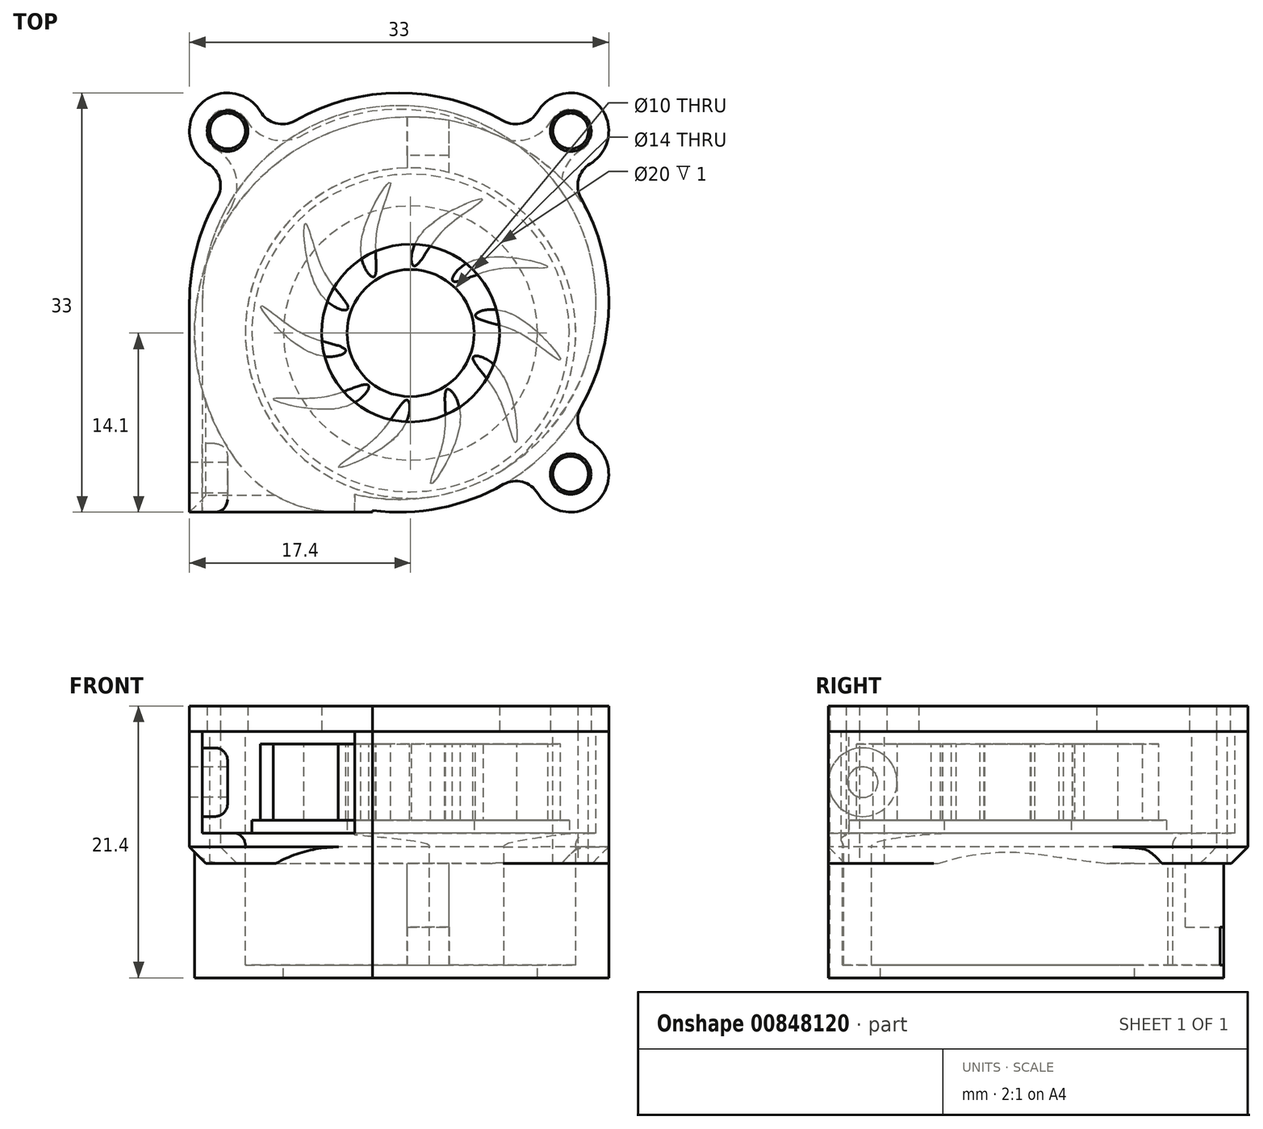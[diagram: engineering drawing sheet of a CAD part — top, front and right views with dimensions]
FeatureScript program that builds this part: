
annotation { "Feature Type Name" : "Feature", "Feature Type Description" : "" }
export const myFeature = defineFeature(function(context is Context, id is Id, definition is map)
    precondition{}
    {
        {
            var Q0;
            Q0=qCreatedBy(makeId("Top.planeOp"),FACE);
            var sketch = newSketch(context, id + "F0", { "sketchPlane" : qUnion([Q0])});
            skLineSegment(sketch, "E0.bottom", {"start": v(-16.5, 16.5) * mm, "end": v(16.5, 16.5) * mm});
            skLineSegment(sketch, "E0.top", {"start": v(-16.5, -16.5) * mm, "end": v(16.5, -16.5) * mm});
            skLineSegment(sketch, "E0.left", {"start": v(-16.5, 16.5) * mm, "end": v(-16.5, -16.5) * mm});
            skLineSegment(sketch, "E0.right", {"start": v(16.5, 16.5) * mm, "end": v(16.5, -16.5) * mm});
            skPoint(sketch, "E0.middle", {"position": v(0, 0) * mm});
            skCircle(sketch, "E1", {"center": v(0.9, -2.4) * mm, "radius": 13 * mm});
            skPoint(sketch, "E2.positionSnap0", {"position": v(0, -16.5) * mm});
            skArc(sketch, "E3", {"start": v(-3.5, -15.1) * mm, "mid": v(12.13, 9.64) * mm, "end": v(-15.5, 0) * mm});
            skLineSegment(sketch, "E4", {"start": v(-15.5, 0) * mm, "end": v(-15.5, -16.5) * mm});
            skLineSegment(sketch, "E5", {"start": v(-3.5, -16.5) * mm, "end": v(-3.5, -15.1) * mm});
            skLineSegment(sketch, "E6.bottom", {"start": v(13.5, 13.5) * mm, "end": v(-13.5, 13.5) * mm, "construction": true});
            skLineSegment(sketch, "E6.top", {"start": v(13.5, -13.5) * mm, "end": v(-13.5, -13.5) * mm, "construction": true});
            skLineSegment(sketch, "E6.left", {"start": v(13.5, 13.5) * mm, "end": v(13.5, -13.5) * mm, "construction": true});
            skLineSegment(sketch, "E6.right", {"start": v(-13.5, 13.5) * mm, "end": v(-13.5, -13.5) * mm, "construction": true});
            skCircle(sketch, "E7", {"center": v(-13.5, 13.5) * mm, "radius": 1.4 * mm});
            skCircle(sketch, "E8", {"center": v(13.5, 13.5) * mm, "radius": 1.4 * mm});
            skCircle(sketch, "E9", {"center": v(13.5, -13.5) * mm, "radius": 1.4 * mm});
            skCircle(sketch, "E10", {"center": v(0.9, -2.4) * mm, "radius": 11.75 * mm, "construction": true});
            skArc(sketch, "E11.0", {"start": v(-2.1, -16.37) * mm, "mid": v(12.39, 10.9) * mm, "end": v(-16.5, 0) * mm});
            skLineSegment(sketch, "E12", {"start": v(-2.1, -16.37) * mm, "end": v(-2.1, -16.5) * mm});
            skArc(sketch, "E13", {"start": v(-10.63, 12.62) * mm, "mid": v(-15.62, 15.62) * mm, "end": v(-12.62, 10.63) * mm});
            skArc(sketch, "E14.1.0", {"start": v(12.62, 10.63) * mm, "mid": v(15.62, 15.62) * mm, "end": v(10.63, 12.62) * mm});
            skArc(sketch, "E14.2.0", {"start": v(10.63, -12.62) * mm, "mid": v(15.62, -15.62) * mm, "end": v(12.62, -10.63) * mm});
            skLineSegment(sketch, "E14.anchor1", {"start": v(0, 0) * mm, "end": v(-12.62, 10.63) * mm, "construction": true});
            skLineSegment(sketch, "E14.anchor2", {"start": v(0, 0) * mm, "end": v(12.62, -10.63) * mm, "construction": true});
            skLineSegment(sketch, "E15", {"start": v(3.93, 10.24) * mm, "end": v(3.93, 11.58) * mm});
            skLineSegment(sketch, "E16", {"start": v(3.93, 11.58) * mm, "end": v(0.64, 11.58) * mm});
            skLineSegment(sketch, "E17", {"start": v(0.64, 11.58) * mm, "end": v(0.64, 10.6) * mm});
            skSolve(sketch);
        }
        {
            var Q0;
            {var subQ0=sQuery(id+"F0.wireOp",EDGE,"8aHMBO7B-eonY-Z6f1-7xxv-SSlK2QK2lGQh");Q0=makeQuery(id+"F0.imprint","IMPRINT",FACE,{"disambiguationData":[TD([[makeQuery(id+"F0.imprint","IMPRINT",EDGE,{"derivedFrom":subQ0}),1.0]])]});}
            var Q1;
            {var subQ0=sQuery(id+"F0.wireOp",EDGE,"mYrk5g2D-YhFv-AHOF-tiMq-TT1jAZq6Yysg");Q1=makeQuery(id+"F0.imprint","IMPRINT",FACE,{"disambiguationData":[TD([[makeQuery(id+"F0.imprint","IMPRINT",EDGE,{"derivedFrom":subQ0}),1.0]])]});}
            var Q2;
            {var subQ0=sQuery(id+"F0.wireOp",EDGE,"RpQWQKDe-v6hF-UeJ0-nlzF-b0iv6W1jkAfd");Q2=makeQuery(id+"F0.imprint","IMPRINT",FACE,{"disambiguationData":[TD([[makeQuery(id+"F0.imprint","IMPRINT",EDGE,{"derivedFrom":subQ0}),-1.0]])]});}
            var Q3;
            Q3=makeQuery(id+"F0.imprint","IMPRINT",FACE,{"disambiguationData":[TD([[makeQuery(id+"F0.imprint","IMPRINT",EDGE,{"derivedFrom":sQuery(id+"F0.wireOp",EDGE,"E7")}),-1.0]])]});
            var Q4;
            Q4=makeQuery(id+"F0.imprint","IMPRINT",FACE,{"disambiguationData":[TD([[makeQuery(id+"F0.imprint","IMPRINT",EDGE,{"derivedFrom":sQuery(id+"F0.wireOp",EDGE,"E3")}),-1.0]])]});
            var Q5;
            Q5=makeQuery(id+"F0.imprint","IMPRINT",FACE,{"disambiguationData":[TD([[makeQuery(id+"F0.imprint","IMPRINT",EDGE,{"derivedFrom":sQuery(id+"F0.wireOp",EDGE,"E8")}),-1.0]])]});
            var Q6;
            Q6=makeQuery(id+"F0.imprint","IMPRINT",FACE,{"disambiguationData":[TD([[makeQuery(id+"F0.imprint","IMPRINT",EDGE,{"derivedFrom":sQuery(id+"F0.wireOp",EDGE,"E9")}),-1.0]])]});
            var Q7;
            Q7=makeQuery(id+"F0.imprint","IMPRINT",FACE,{"disambiguationData":[TD([[makeQuery(id+"F0.imprint","IMPRINT",EDGE,{"derivedFrom":sQuery(id+"F0.wireOp",EDGE,"E3")}),1.0]])]});
            var Q8;
            {var subQ0=sQuery(id+"F0.wireOp",EDGE,"E15");Q8=makeQuery(id+"F0.imprint","IMPRINT",FACE,{"disambiguationData":[TD([[makeQuery(id+"F0.imprint","IMPRINT",EDGE,{"derivedFrom":subQ0}),1.0]])]});}
            var Q9;
            {var subQ5=sQuery(id+"F0.wireOp",EDGE,"E4");Q9=makeQuery(id+"F0.imprint","IMPRINT",FACE,{"disambiguationData":[TD([[makeQuery(id+"F0.imprint","IMPRINT",EDGE,{"derivedFrom":subQ5}),-1.0]])]});}
            extrude(context, id + "F1", {"entities" : qUnion([Q0, Q1, Q2, Q3, Q4, Q5, Q6, Q7, Q8, Q9]), "oppositeDirection" : true, "depth" : 2.4 * mm, "offsetDistance" : 25 * mm});
        }
        {
            var Q0;
            Q0=makeQuery(id+"F0.imprint","IMPRINT",FACE,{"disambiguationData":[TD([[makeQuery(id+"F0.imprint","IMPRINT",EDGE,{"derivedFrom":sQuery(id+"F0.wireOp",EDGE,"E7")}),-1.0]])]});
            var Q1;
            Q1=makeQuery(id+"F0.imprint","IMPRINT",FACE,{"disambiguationData":[TD([[makeQuery(id+"F0.imprint","IMPRINT",EDGE,{"derivedFrom":sQuery(id+"F0.wireOp",EDGE,"E3")}),-1.0]])]});
            var Q2;
            Q2=makeQuery(id+"F0.imprint","IMPRINT",FACE,{"disambiguationData":[TD([[makeQuery(id+"F0.imprint","IMPRINT",EDGE,{"derivedFrom":sQuery(id+"F0.wireOp",EDGE,"E9")}),-1.0]])]});
            var Q3;
            Q3=makeQuery(id+"F0.imprint","IMPRINT",FACE,{"disambiguationData":[TD([[makeQuery(id+"F0.imprint","IMPRINT",EDGE,{"derivedFrom":sQuery(id+"F0.wireOp",EDGE,"E8")}),-1.0]])]});
            var Q4;
            {var subQ5=sQuery(id+"F0.wireOp",EDGE,"E4");Q4=makeQuery(id+"F0.imprint","IMPRINT",FACE,{"disambiguationData":[TD([[makeQuery(id+"F0.imprint","IMPRINT",EDGE,{"derivedFrom":subQ5}),-1.0]])]});}
            extrude(context, id + "F2", {"entities" : qUnion([Q0, Q1, Q2, Q3, Q4]), "operationType" : NewBodyOperationType.ADD, "depth" : 8 * mm, "offsetDistance" : 25 * mm});
        }
        {
            var Q0;
            Q0=makeQuery(id+"F1.opExtrude","CAP_FACE",FACE,{"disambiguationData":[OSD([sQuery(id+"F0.wireOp",EDGE,"E0.bottom"),sQuery(id+"F0.wireOp",EDGE,"E0.top"),sQuery(id+"F0.wireOp",EDGE,"E0.left"),sQuery(id+"F0.wireOp",EDGE,"E0.right"),sQuery(id+"F0.wireOp",EDGE,"E1"),sQuery(id+"F0.wireOp",EDGE,"E7"),sQuery(id+"F0.wireOp",EDGE,"E8"),sQuery(id+"F0.wireOp",EDGE,"E9")])],"isStart":false});
            var sketch = newSketch(context, id + "F3", { "sketchPlane" : qUnion([Q0])});
            skCircle(sketch, "E18.0", {"center": v(0.9, 2.4) * mm, "radius": 17 * mm});
            skArc(sketch, "E19.0", {"start": v(-2.1, 16.37) * mm, "mid": v(12.39, -10.9) * mm, "end": v(-16.5, 0) * mm});
            skLineSegment(sketch, "E20.0", {"start": v(3.93, -11.58) * mm, "end": v(0.64, -11.58) * mm});
            skLineSegment(sketch, "E21.0", {"start": v(3.93, -10.24) * mm, "end": v(3.93, -11.58) * mm});
            skPoint(sketch, "E22.0", {"position": v(0.64, -11.09) * mm});
            skLineSegment(sketch, "E23.0", {"start": v(0.64, -11.58) * mm, "end": v(0.64, -10.6) * mm});
            skSolve(sketch);
        }
        {
            var Q0;
            Q0=makeQuery(id+"F3.imprint","IMPRINT",FACE,{"disambiguationData":[TD([[makeQuery(id+"F3.imprint","IMPRINT",EDGE,{"derivedFrom":sQuery(id+"F3.wireOp",EDGE,"E20.0")}),1.0]])]});
            extrude(context, id + "F4", {"entities" : qUnion([Q0]), "operationType" : NewBodyOperationType.ADD, "depth" : 8 * mm, "offsetDistance" : 25 * mm});
        }
        {
            var Q0;
            {var subQ0=sQuery(id+"F0.wireOp",EDGE,"E13");var subQ1=sQuery(id+"F0.wireOp",EDGE,"E11.0");var subQ2=makeQuery(id+"F0.imprint","INTERSECT",VERTEX,{"disambiguationData":[OD(1.0)],"derivedFrom":[subQ1,subQ0]});Q0=makeQuery(id+"F2.boolean.opBoolean","MERGE",EDGE,{"derivedFrom":[makeQuery(id+"F1.opExtrude","SWEPT_EDGE",EDGE,{"disambiguationData":[OSD([subQ1,subQ0]),TDD([subQ2])]}),makeQuery(id+"F2.opExtrude","SWEPT_EDGE",EDGE,{"disambiguationData":[OSD([subQ1,subQ0]),TDD([subQ2])]})]});}
            var Q1;
            {var subQ0=sQuery(id+"F0.wireOp",EDGE,"E13");var subQ1=sQuery(id+"F0.wireOp",EDGE,"E11.0");var subQ2=makeQuery(id+"F0.imprint","INTERSECT",VERTEX,{"disambiguationData":[OD(0.0)],"derivedFrom":[subQ1,subQ0]});Q1=makeQuery(id+"F2.boolean.opBoolean","MERGE",EDGE,{"derivedFrom":[makeQuery(id+"F1.opExtrude","SWEPT_EDGE",EDGE,{"disambiguationData":[OSD([subQ1,subQ0]),TDD([subQ2])]}),makeQuery(id+"F2.opExtrude","SWEPT_EDGE",EDGE,{"disambiguationData":[OSD([subQ1,subQ0]),TDD([subQ2])]})]});}
            var Q2;
            {var subQ0=sQuery(id+"F0.wireOp",EDGE,"E14.1.0");var subQ1=sQuery(id+"F0.wireOp",EDGE,"E11.0");var subQ2=makeQuery(id+"F0.imprint","INTERSECT",VERTEX,{"disambiguationData":[OD(1.0)],"derivedFrom":[subQ1,subQ0]});Q2=makeQuery(id+"F2.boolean.opBoolean","MERGE",EDGE,{"derivedFrom":[makeQuery(id+"F1.opExtrude","SWEPT_EDGE",EDGE,{"disambiguationData":[OSD([subQ1,subQ0]),TDD([subQ2])]}),makeQuery(id+"F2.opExtrude","SWEPT_EDGE",EDGE,{"disambiguationData":[OSD([subQ1,subQ0]),TDD([subQ2])]})]});}
            var Q3;
            {var subQ0=sQuery(id+"F0.wireOp",EDGE,"E14.1.0");var subQ1=sQuery(id+"F0.wireOp",EDGE,"E11.0");var subQ2=makeQuery(id+"F0.imprint","INTERSECT",VERTEX,{"disambiguationData":[OD(0.0)],"derivedFrom":[subQ1,subQ0]});Q3=makeQuery(id+"F2.boolean.opBoolean","MERGE",EDGE,{"derivedFrom":[makeQuery(id+"F1.opExtrude","SWEPT_EDGE",EDGE,{"disambiguationData":[OSD([subQ1,subQ0]),TDD([subQ2])]}),makeQuery(id+"F2.opExtrude","SWEPT_EDGE",EDGE,{"disambiguationData":[OSD([subQ1,subQ0]),TDD([subQ2])]})]});}
            var Q4;
            {var subQ0=sQuery(id+"F0.wireOp",EDGE,"E14.2.0");var subQ1=sQuery(id+"F0.wireOp",EDGE,"E11.0");var subQ2=makeQuery(id+"F0.imprint","INTERSECT",VERTEX,{"disambiguationData":[OD(0.0)],"derivedFrom":[subQ1,subQ0]});Q4=makeQuery(id+"F2.boolean.opBoolean","MERGE",EDGE,{"derivedFrom":[makeQuery(id+"F1.opExtrude","SWEPT_EDGE",EDGE,{"disambiguationData":[OSD([subQ1,subQ0]),TDD([subQ2])]}),makeQuery(id+"F2.opExtrude","SWEPT_EDGE",EDGE,{"disambiguationData":[OSD([subQ1,subQ0]),TDD([subQ2])]})]});}
            var Q5;
            {var subQ0=sQuery(id+"F0.wireOp",EDGE,"E14.2.0");var subQ1=sQuery(id+"F0.wireOp",EDGE,"E11.0");var subQ2=makeQuery(id+"F0.imprint","INTERSECT",VERTEX,{"disambiguationData":[OD(1.0)],"derivedFrom":[subQ1,subQ0]});Q5=makeQuery(id+"F2.boolean.opBoolean","MERGE",EDGE,{"derivedFrom":[makeQuery(id+"F1.opExtrude","SWEPT_EDGE",EDGE,{"disambiguationData":[OSD([subQ1,subQ0]),TDD([subQ2])]}),makeQuery(id+"F2.opExtrude","SWEPT_EDGE",EDGE,{"disambiguationData":[OSD([subQ1,subQ0]),TDD([subQ2])]})]});}
            fillet(context, id + "F5", {"entities" : qUnion([Q0, Q1, Q2, Q3, Q4, Q5]), "radius" : 2 * mm, "tangentPropagation" : true, "allowEdgeOverflow" : false});
        }
        {
            var Q0;
            Q0=makeQuery(id+"F2.opExtrude","CAP_FACE",FACE,{"disambiguationData":[OSD([sQuery(id+"F0.wireOp",EDGE,"E0.bottom"),sQuery(id+"F0.wireOp",EDGE,"E0.top"),sQuery(id+"F0.wireOp",EDGE,"E0.left"),sQuery(id+"F0.wireOp",EDGE,"E0.right"),sQuery(id+"F0.wireOp",EDGE,"E3"),sQuery(id+"F0.wireOp",EDGE,"E4"),sQuery(id+"F0.wireOp",EDGE,"E5"),sQuery(id+"F0.wireOp",EDGE,"E7"),sQuery(id+"F0.wireOp",EDGE,"E8"),sQuery(id+"F0.wireOp",EDGE,"E9")])],"isStart":false});
            var sketch = newSketch(context, id + "F6", { "sketchPlane" : qUnion([Q0])});
            skPoint(sketch, "E24.0", {"position": v(0.9, -2.4) * mm});
            skCircle(sketch, "E25", {"center": v(13.5, 13.5) * mm, "radius": 1.6 * mm});
            skCircle(sketch, "E26", {"center": v(13.5, -13.5) * mm, "radius": 1.6 * mm});
            skCircle(sketch, "E27", {"center": v(-13.5, 13.5) * mm, "radius": 1.6 * mm});
            skArc(sketch, "E28.0.0", {"start": v(8.2, 14.32) * mm, "mid": v(0, 16.5) * mm, "end": v(-8.2, 14.32) * mm});
            skArc(sketch, "E28.0.1", {"start": v(-8.2, 14.32) * mm, "mid": v(-9.7, 14.12) * mm, "end": v(-10.92, 15.03) * mm});
            skArc(sketch, "E28.0.2", {"start": v(-10.92, 15.03) * mm, "mid": v(-15.62, 15.62) * mm, "end": v(-15.03, 10.92) * mm});
            skArc(sketch, "E28.0.3", {"start": v(-15.03, 10.92) * mm, "mid": v(-14.12, 9.7) * mm, "end": v(-14.32, 8.2) * mm});
            skArc(sketch, "E28.0.4", {"start": v(-14.32, 8.2) * mm, "mid": v(-15.94, 4.25) * mm, "end": v(-16.5, 0) * mm});
            skLineSegment(sketch, "E28.0.5", {"start": v(-16.5, 0) * mm, "end": v(-16.5, -16.5) * mm});
            skLineSegment(sketch, "E28.0.6", {"start": v(-16.5, -16.5) * mm, "end": v(-15.5, -16.5) * mm});
            skLineSegment(sketch, "E28.0.10", {"start": v(-3.5, -16.5) * mm, "end": v(-2.1, -16.5) * mm});
            skLineSegment(sketch, "E28.0.11", {"start": v(-2.1, -16.5) * mm, "end": v(-2.1, -16.37) * mm});
            skArc(sketch, "E28.0.12", {"start": v(-2.1, -16.37) * mm, "mid": v(3.22, -16.18) * mm, "end": v(8.2, -14.32) * mm});
            skArc(sketch, "E28.0.13", {"start": v(8.2, -14.32) * mm, "mid": v(9.7, -14.12) * mm, "end": v(10.92, -15.03) * mm});
            skArc(sketch, "E28.0.14", {"start": v(10.92, -15.03) * mm, "mid": v(15.62, -15.62) * mm, "end": v(15.03, -10.92) * mm});
            skArc(sketch, "E28.0.15", {"start": v(15.03, -10.92) * mm, "mid": v(14.12, -9.7) * mm, "end": v(14.32, -8.2) * mm});
            skArc(sketch, "E28.0.16", {"start": v(14.32, -8.2) * mm, "mid": v(16.5, 0) * mm, "end": v(14.32, 8.2) * mm});
            skArc(sketch, "E28.0.17", {"start": v(14.32, 8.2) * mm, "mid": v(14.12, 9.7) * mm, "end": v(15.03, 10.92) * mm});
            skArc(sketch, "E28.0.18", {"start": v(15.03, 10.92) * mm, "mid": v(15.62, 15.62) * mm, "end": v(10.92, 15.03) * mm});
            skArc(sketch, "E28.0.19", {"start": v(10.92, 15.03) * mm, "mid": v(9.7, 14.12) * mm, "end": v(8.2, 14.32) * mm});
            skLineSegment(sketch, "E29", {"start": v(-3.5, -16.5) * mm, "end": v(-15.5, -16.5) * mm});
            skLineSegment(sketch, "E30", {"start": v(-0.39, -2.4) * mm, "end": v(-0.39, -2.69) * mm});
            skLineSegment(sketch, "E31", {"start": v(-0.39, -2.69) * mm, "end": v(-4.7, -4.54) * mm});
            skLineSegment(sketch, "E32", {"start": v(-4.7, -4.54) * mm, "end": v(-4.7, -2.4) * mm});
            skLineSegment(sketch, "E33", {"start": v(-4.7, -2.4) * mm, "end": v(-0.39, -2.4) * mm, "construction": true});
            skLineSegment(sketch, "E34.MirrorCS", {"start": v(-4.7, -0.26) * mm, "end": v(-4.7, -2.4) * mm});
            skLineSegment(sketch, "E35.MirrorCS", {"start": v(-0.39, -2.11) * mm, "end": v(-4.7, -0.26) * mm});
            skLineSegment(sketch, "E36.MirrorCS", {"start": v(-0.39, -2.4) * mm, "end": v(-0.39, -2.11) * mm});
            skLineSegment(sketch, "E37.1.0", {"start": v(-0.13, -3.23) * mm, "end": v(-4.27, -5.44) * mm});
            skLineSegment(sketch, "E37.1.1", {"start": v(0.1, -3.4) * mm, "end": v(0.32, -3.59) * mm});
            skLineSegment(sketch, "E37.1.2", {"start": v(0.1, -3.4) * mm, "end": v(-0.13, -3.23) * mm});
            skLineSegment(sketch, "E37.1.3", {"start": v(0.32, -3.59) * mm, "end": v(-0.92, -8.12) * mm});
            skLineSegment(sketch, "E37.1.4", {"start": v(-0.92, -8.12) * mm, "end": v(-2.6, -6.78) * mm});
            skLineSegment(sketch, "E37.1.5", {"start": v(-4.27, -5.44) * mm, "end": v(-2.6, -6.78) * mm});
            skLineSegment(sketch, "E37.2.0", {"start": v(0.9, -3.72) * mm, "end": v(0.06, -8.34) * mm});
            skLineSegment(sketch, "E37.2.1", {"start": v(1.19, -3.66) * mm, "end": v(1.47, -3.6) * mm});
            skLineSegment(sketch, "E37.2.2", {"start": v(1.19, -3.66) * mm, "end": v(0.9, -3.72) * mm});
            skLineSegment(sketch, "E37.2.3", {"start": v(1.47, -3.6) * mm, "end": v(4.24, -7.39) * mm});
            skLineSegment(sketch, "E37.2.4", {"start": v(4.24, -7.39) * mm, "end": v(2.15, -7.86) * mm});
            skLineSegment(sketch, "E37.2.5", {"start": v(0.06, -8.34) * mm, "end": v(2.15, -7.86) * mm});
            skLineSegment(sketch, "E37.3.0", {"start": v(1.94, -3.22) * mm, "end": v(5.02, -6.76) * mm});
            skLineSegment(sketch, "E37.3.1", {"start": v(2.06, -2.96) * mm, "end": v(2.19, -2.7) * mm});
            skLineSegment(sketch, "E37.3.2", {"start": v(2.06, -2.96) * mm, "end": v(1.94, -3.22) * mm});
            skLineSegment(sketch, "E37.3.3", {"start": v(2.19, -2.7) * mm, "end": v(6.88, -2.9) * mm});
            skLineSegment(sketch, "E37.3.4", {"start": v(6.88, -2.9) * mm, "end": v(5.95, -4.83) * mm});
            skLineSegment(sketch, "E37.3.5", {"start": v(5.02, -6.76) * mm, "end": v(5.95, -4.83) * mm});
            skLineSegment(sketch, "E37.4.0", {"start": v(2.19, -2.1) * mm, "end": v(6.88, -1.9) * mm});
            skLineSegment(sketch, "E37.4.1", {"start": v(2.06, -1.84) * mm, "end": v(1.94, -1.58) * mm});
            skLineSegment(sketch, "E37.4.2", {"start": v(2.06, -1.84) * mm, "end": v(2.19, -2.1) * mm});
            skLineSegment(sketch, "E37.4.3", {"start": v(1.94, -1.58) * mm, "end": v(5.02, 1.96) * mm});
            skLineSegment(sketch, "E37.4.4", {"start": v(5.02, 1.96) * mm, "end": v(5.95, 0.03) * mm});
            skLineSegment(sketch, "E37.4.5", {"start": v(6.88, -1.9) * mm, "end": v(5.95, 0.03) * mm});
            skLineSegment(sketch, "E37.5.0", {"start": v(1.47, -1.2) * mm, "end": v(4.24, 2.59) * mm});
            skLineSegment(sketch, "E37.5.1", {"start": v(1.19, -1.14) * mm, "end": v(0.9, -1.08) * mm});
            skLineSegment(sketch, "E37.5.2", {"start": v(1.19, -1.14) * mm, "end": v(1.47, -1.2) * mm});
            skLineSegment(sketch, "E37.5.3", {"start": v(0.9, -1.08) * mm, "end": v(0.06, 3.54) * mm});
            skLineSegment(sketch, "E37.5.4", {"start": v(0.06, 3.54) * mm, "end": v(2.15, 3.06) * mm});
            skLineSegment(sketch, "E37.5.5", {"start": v(4.24, 2.59) * mm, "end": v(2.15, 3.06) * mm});
            skLineSegment(sketch, "E37.6.0", {"start": v(0.32, -1.21) * mm, "end": v(-0.92, 3.32) * mm});
            skLineSegment(sketch, "E37.6.1", {"start": v(0.1, -1.4) * mm, "end": v(-0.13, -1.57) * mm});
            skLineSegment(sketch, "E37.6.2", {"start": v(0.1, -1.4) * mm, "end": v(0.32, -1.21) * mm});
            skLineSegment(sketch, "E37.6.3", {"start": v(-0.13, -1.57) * mm, "end": v(-4.27, 0.64) * mm});
            skLineSegment(sketch, "E37.6.4", {"start": v(-4.27, 0.64) * mm, "end": v(-2.6, 1.98) * mm});
            skLineSegment(sketch, "E37.6.5", {"start": v(-0.92, 3.32) * mm, "end": v(-2.6, 1.98) * mm});
            skCircle(sketch, "E38", {"center": v(0.9, -2.4) * mm, "radius": 7 * mm});
            skSolve(sketch);
        }
        {
            var Q0;
            Q0=qSketchRegion(id+"F6",true);
            extrude(context, id + "F7", {"entities" : qUnion([Q0]), "depth" : 2 * mm, "offsetDistance" : 25 * mm});
        }
        {
            var Q0;
            Q0=makeQuery(id+"F1.opExtrude","CAP_FACE",FACE,{"disambiguationData":[OSD([sQuery(id+"F0.wireOp",EDGE,"E0.top"),sQuery(id+"F0.wireOp",EDGE,"E0.left"),sQuery(id+"F0.wireOp",EDGE,"E1"),sQuery(id+"F0.wireOp",EDGE,"E7"),sQuery(id+"F0.wireOp",EDGE,"E8"),sQuery(id+"F0.wireOp",EDGE,"E9"),sQuery(id+"F0.wireOp",EDGE,"E11.0"),sQuery(id+"F0.wireOp",EDGE,"E12"),sQuery(id+"F0.wireOp",EDGE,"E13"),sQuery(id+"F0.wireOp",EDGE,"E14.1.0"),sQuery(id+"F0.wireOp",EDGE,"E14.2.0"),sQuery(id+"F0.wireOp",EDGE,"E15"),sQuery(id+"F0.wireOp",EDGE,"E16"),sQuery(id+"F0.wireOp",EDGE,"E17")])],"isStart":true});
            var sketch = newSketch(context, id + "F8", { "sketchPlane" : qUnion([Q0])});
            skPoint(sketch, "E39.0", {"position": v(0.9, -2.4) * mm});
            skCircle(sketch, "E40", {"center": v(0.9, -2.4) * mm, "radius": 1.25 * mm});
            skCircle(sketch, "E41", {"center": v(0.9, -2.4) * mm, "radius": 5 * mm});
            skCircle(sketch, "E42", {"center": v(0.9, -2.4) * mm, "radius": 12.5 * mm});
            skPoint(sketch, "E43.4.internal.snap0", {"position": v(0, 3.58) * mm});
            skFitSpline(sketch, "E43", {"points": [v(1.17, 2.88) * mm, v(1.72, 5.4) * mm, v(6.58, 8.17) * mm, v(4.56, 6.6) * mm, v(2.47, 4.44) * mm, v(1.17, 2.88) * mm]});
            skSolve(sketch);
        }
        {
            var Q0;
            {var subQ0=sQuery(id+"F8.wireOp",EDGE,"E43");var subQ1=sQuery(id+"F8.wireOp",EDGE,"E42");var subQ2=makeQuery(id+"F8.imprint","INTERSECT",VERTEX,{"disambiguationData":[OD(0.0)],"derivedFrom":[subQ1,subQ0]});Q0=makeQuery(id+"F8.imprint","IMPRINT",FACE,{"disambiguationData":[TD([[makeQuery(id+"F8.imprint","IMPRINT",EDGE,{"disambiguationData":[TD([[subQ2,1.0]])],"derivedFrom":subQ1}),-1.0]])]});}
            var Q1;
            Q1=makeQuery(id+"F8.imprint","IMPRINT",FACE,{"disambiguationData":[TD([[makeQuery(id+"F8.imprint","IMPRINT",EDGE,{"derivedFrom":sQuery(id+"F8.wireOp",EDGE,"E43")}),-1.0]])]});
            extrude(context, id + "F9", {"entities" : qUnion([Q0, Q1]), "depth" : 7 * mm, "offsetDistance" : 25 * mm});
        }
        {
            var Q0;
            Q0=makeQuery(id+"F8.imprint","IMPRINT",FACE,{"disambiguationData":[TD([[makeQuery(id+"F8.imprint","IMPRINT",EDGE,{"derivedFrom":sQuery(id+"F8.wireOp",EDGE,"E41")}),-1.0]])]});
            extrude(context, id + "F10", {"entities" : qUnion([Q0]), "depth" : 1 * mm, "offsetDistance" : 25 * mm});
        }
        {
            var Q0;
            Q0=makeQuery(id+"F9.opExtrude","SWEPT_BODY",BODY,{"disambiguationData":[OSD([sQuery(id+"F8.wireOp",EDGE,"E43")])]});
            var Q1;
            Q1=sQuery(id+"F8.wireOp",EDGE,"E42");
            circularPattern(context, id + "F11", {"operationType" : NewBodyOperationType.ADD, "entities" : qUnion([Q0]), "axis" : qUnion([Q1]), "angle" : 360 * degree, "instanceCount" : 10, "equalSpace" : true});
        }
        {
            var Q0;
            Q0=makeQuery(id+"F1.opExtrude","CAP_EDGE",EDGE,{"disambiguationData":[OSD([sQuery(id+"F0.wireOp",EDGE,"E14.1.0")])],"isStart":false});
            var Q1;
            {var subQ0=sQuery(id+"F0.wireOp",EDGE,"E11.0");Q1=makeQuery(id+"F1.opExtrude","CAP_EDGE",EDGE,{"disambiguationData":[OSD([subQ0]),TDD([makeQuery(id+"F0.imprint","IMPRINT",EDGE,{"disambiguationData":[TD([[makeQuery(id+"F0.imprint","INTERSECT",VERTEX,{"disambiguationData":[OD(1.0)],"derivedFrom":[subQ0,sQuery(id+"F0.wireOp",EDGE,"E14.1.0")]}),-1.0]])],"derivedFrom":subQ0}),makeQuery(id+"F0.imprint","IMPRINT",EDGE,{"disambiguationData":[TD([[makeQuery(id+"F0.imprint","INTERSECT",VERTEX,{"disambiguationData":[OD(0.0)],"derivedFrom":[subQ0,sQuery(id+"F0.wireOp",EDGE,"E13")]}),1.0]])],"derivedFrom":subQ0})])],"isStart":false});}
            var Q2;
            {var subQ0=sQuery(id+"F0.wireOp",EDGE,"E13");var subQ1=sQuery(id+"F0.wireOp",EDGE,"E11.0");var subQ4=sQuery(id+"F0.wireOp",EDGE,"E14.1.0");var subQ5=makeQuery(id+"F0.imprint","INTERSECT",VERTEX,{"disambiguationData":[OD(1.0)],"derivedFrom":[subQ1,subQ4]});var subQ9=sQuery(id+"F0.wireOp",EDGE,"E14.2.0");var subQ11=sQuery(id+"F0.wireOp",EDGE,"E0.top");var subQ14=sQuery(id+"F0.wireOp",EDGE,"E12");var subQ16=sQuery(id+"F0.wireOp",EDGE,"E8");var subQ17=sQuery(id+"F0.wireOp",EDGE,"E7");var subQ18=sQuery(id+"F0.wireOp",EDGE,"E0.left");Q2=makeQuery(id+"F5.opFillet","BLEND_EDGE",EDGE,{"blendedFrom":[makeQuery(id+"F2.boolean.opBoolean","MERGE",EDGE,{"derivedFrom":[makeQuery(id+"F1.opExtrude","SWEPT_EDGE",EDGE,{"disambiguationData":[OSD([subQ1,subQ4]),TDD([subQ5])]}),makeQuery(id+"F2.opExtrude","SWEPT_EDGE",EDGE,{"disambiguationData":[OSD([subQ1,subQ4]),TDD([subQ5])]})]}),makeQuery(id+"F4.boolean.opBoolean","SPLIT",FACE,{"disambiguationData":[TD([makeQuery(id+"F1.opExtrude","SWEPT_FACE",FACE,{"disambiguationData":[OSD([subQ11])]})])],"derivedFrom":makeQuery(id+"F1.opExtrude","CAP_FACE",FACE,{"disambiguationData":[OSD([subQ11,subQ18,sQuery(id+"F0.wireOp",EDGE,"E1"),subQ17,subQ16,sQuery(id+"F0.wireOp",EDGE,"E9"),subQ1,subQ14,subQ0,subQ4,subQ9])],"isStart":false})})],"blendedInto":[makeQuery(id+"F4.boolean.opBoolean","SPLIT",FACE,{"disambiguationData":[TD([makeQuery(id+"F1.opExtrude","SWEPT_FACE",FACE,{"disambiguationData":[OSD([subQ11])]})])],"derivedFrom":makeQuery(id+"F1.opExtrude","CAP_FACE",FACE,{"disambiguationData":[OSD([subQ11,subQ18,sQuery(id+"F0.wireOp",EDGE,"E1"),subQ17,subQ16,sQuery(id+"F0.wireOp",EDGE,"E9"),subQ1,subQ14,subQ0,subQ4,subQ9])],"isStart":false})})]});}
            var Q3;
            {var subQ0=sQuery(id+"F0.wireOp",EDGE,"E13");var subQ1=sQuery(id+"F0.wireOp",EDGE,"E11.0");var subQ4=sQuery(id+"F0.wireOp",EDGE,"E14.1.0");var subQ6=makeQuery(id+"F0.imprint","INTERSECT",VERTEX,{"disambiguationData":[OD(0.0)],"derivedFrom":[subQ1,subQ4]});var subQ9=sQuery(id+"F0.wireOp",EDGE,"E14.2.0");var subQ11=sQuery(id+"F0.wireOp",EDGE,"E0.top");var subQ14=sQuery(id+"F0.wireOp",EDGE,"E12");var subQ16=sQuery(id+"F0.wireOp",EDGE,"E8");var subQ17=sQuery(id+"F0.wireOp",EDGE,"E7");var subQ18=sQuery(id+"F0.wireOp",EDGE,"E0.left");Q3=makeQuery(id+"F5.opFillet","BLEND_EDGE",EDGE,{"blendedFrom":[makeQuery(id+"F2.boolean.opBoolean","MERGE",EDGE,{"derivedFrom":[makeQuery(id+"F1.opExtrude","SWEPT_EDGE",EDGE,{"disambiguationData":[OSD([subQ1,subQ4]),TDD([subQ6])]}),makeQuery(id+"F2.opExtrude","SWEPT_EDGE",EDGE,{"disambiguationData":[OSD([subQ1,subQ4]),TDD([subQ6])]})]}),makeQuery(id+"F4.boolean.opBoolean","SPLIT",FACE,{"disambiguationData":[TD([makeQuery(id+"F1.opExtrude","SWEPT_FACE",FACE,{"disambiguationData":[OSD([subQ11])]})])],"derivedFrom":makeQuery(id+"F1.opExtrude","CAP_FACE",FACE,{"disambiguationData":[OSD([subQ11,subQ18,sQuery(id+"F0.wireOp",EDGE,"E1"),subQ17,subQ16,sQuery(id+"F0.wireOp",EDGE,"E9"),subQ1,subQ14,subQ0,subQ4,subQ9])],"isStart":false})})],"blendedInto":[makeQuery(id+"F4.boolean.opBoolean","SPLIT",FACE,{"disambiguationData":[TD([makeQuery(id+"F1.opExtrude","SWEPT_FACE",FACE,{"disambiguationData":[OSD([subQ11])]})])],"derivedFrom":makeQuery(id+"F1.opExtrude","CAP_FACE",FACE,{"disambiguationData":[OSD([subQ11,subQ18,sQuery(id+"F0.wireOp",EDGE,"E1"),subQ17,subQ16,sQuery(id+"F0.wireOp",EDGE,"E9"),subQ1,subQ14,subQ0,subQ4,subQ9])],"isStart":false})})]});}
            var Q4;
            {var subQ0=sQuery(id+"F0.wireOp",EDGE,"E13");var subQ1=sQuery(id+"F0.wireOp",EDGE,"E11.0");var subQ2=makeQuery(id+"F0.imprint","INTERSECT",VERTEX,{"disambiguationData":[OD(0.0)],"derivedFrom":[subQ1,subQ0]});var subQ5=sQuery(id+"F0.wireOp",EDGE,"E14.1.0");var subQ9=sQuery(id+"F0.wireOp",EDGE,"E14.2.0");var subQ11=sQuery(id+"F0.wireOp",EDGE,"E0.top");var subQ14=sQuery(id+"F0.wireOp",EDGE,"E12");var subQ16=sQuery(id+"F0.wireOp",EDGE,"E8");var subQ17=sQuery(id+"F0.wireOp",EDGE,"E7");var subQ18=sQuery(id+"F0.wireOp",EDGE,"E0.left");Q4=makeQuery(id+"F5.opFillet","BLEND_EDGE",EDGE,{"blendedFrom":[makeQuery(id+"F2.boolean.opBoolean","MERGE",EDGE,{"derivedFrom":[makeQuery(id+"F1.opExtrude","SWEPT_EDGE",EDGE,{"disambiguationData":[OSD([subQ1,subQ0]),TDD([subQ2])]}),makeQuery(id+"F2.opExtrude","SWEPT_EDGE",EDGE,{"disambiguationData":[OSD([subQ1,subQ0]),TDD([subQ2])]})]}),makeQuery(id+"F4.boolean.opBoolean","SPLIT",FACE,{"disambiguationData":[TD([makeQuery(id+"F1.opExtrude","SWEPT_FACE",FACE,{"disambiguationData":[OSD([subQ11])]})])],"derivedFrom":makeQuery(id+"F1.opExtrude","CAP_FACE",FACE,{"disambiguationData":[OSD([subQ11,subQ18,sQuery(id+"F0.wireOp",EDGE,"E1"),subQ17,subQ16,sQuery(id+"F0.wireOp",EDGE,"E9"),subQ1,subQ14,subQ0,subQ5,subQ9])],"isStart":false})})],"blendedInto":[makeQuery(id+"F4.boolean.opBoolean","SPLIT",FACE,{"disambiguationData":[TD([makeQuery(id+"F1.opExtrude","SWEPT_FACE",FACE,{"disambiguationData":[OSD([subQ11])]})])],"derivedFrom":makeQuery(id+"F1.opExtrude","CAP_FACE",FACE,{"disambiguationData":[OSD([subQ11,subQ18,sQuery(id+"F0.wireOp",EDGE,"E1"),subQ17,subQ16,sQuery(id+"F0.wireOp",EDGE,"E9"),subQ1,subQ14,subQ0,subQ5,subQ9])],"isStart":false})})]});}
            var Q5;
            Q5=makeQuery(id+"F1.opExtrude","CAP_EDGE",EDGE,{"disambiguationData":[OSD([sQuery(id+"F0.wireOp",EDGE,"E13")])],"isStart":false});
            var Q6;
            {var subQ0=sQuery(id+"F0.wireOp",EDGE,"E11.0");Q6=makeQuery(id+"F1.opExtrude","CAP_EDGE",EDGE,{"disambiguationData":[OSD([subQ0]),TDD([makeQuery(id+"F0.imprint","IMPRINT",EDGE,{"disambiguationData":[TD([[makeQuery(id+"F0.imprint","INTERSECT",VERTEX,{"derivedFrom":[sQuery(id+"F0.wireOp",EDGE,"E0.left"),subQ0]}),1.0]])],"derivedFrom":subQ0})])],"isStart":false});}
            var Q7;
            {var subQ0=sQuery(id+"F0.wireOp",EDGE,"E13");var subQ1=sQuery(id+"F0.wireOp",EDGE,"E11.0");var subQ4=sQuery(id+"F0.wireOp",EDGE,"E14.1.0");var subQ8=sQuery(id+"F0.wireOp",EDGE,"E14.2.0");var subQ10=sQuery(id+"F0.wireOp",EDGE,"E0.top");var subQ13=sQuery(id+"F0.wireOp",EDGE,"E12");var subQ15=sQuery(id+"F0.wireOp",EDGE,"E8");var subQ16=sQuery(id+"F0.wireOp",EDGE,"E7");var subQ17=sQuery(id+"F0.wireOp",EDGE,"E0.left");var subQ18=makeQuery(id+"F0.imprint","INTERSECT",VERTEX,{"disambiguationData":[OD(1.0)],"derivedFrom":[subQ1,subQ0]});Q7=makeQuery(id+"F5.opFillet","BLEND_EDGE",EDGE,{"blendedFrom":[makeQuery(id+"F2.boolean.opBoolean","MERGE",EDGE,{"derivedFrom":[makeQuery(id+"F1.opExtrude","SWEPT_EDGE",EDGE,{"disambiguationData":[OSD([subQ1,subQ0]),TDD([subQ18])]}),makeQuery(id+"F2.opExtrude","SWEPT_EDGE",EDGE,{"disambiguationData":[OSD([subQ1,subQ0]),TDD([subQ18])]})]}),makeQuery(id+"F4.boolean.opBoolean","SPLIT",FACE,{"disambiguationData":[TD([makeQuery(id+"F1.opExtrude","SWEPT_FACE",FACE,{"disambiguationData":[OSD([subQ10])]})])],"derivedFrom":makeQuery(id+"F1.opExtrude","CAP_FACE",FACE,{"disambiguationData":[OSD([subQ10,subQ17,sQuery(id+"F0.wireOp",EDGE,"E1"),subQ16,subQ15,sQuery(id+"F0.wireOp",EDGE,"E9"),subQ1,subQ13,subQ0,subQ4,subQ8])],"isStart":false})})],"blendedInto":[makeQuery(id+"F4.boolean.opBoolean","SPLIT",FACE,{"disambiguationData":[TD([makeQuery(id+"F1.opExtrude","SWEPT_FACE",FACE,{"disambiguationData":[OSD([subQ10])]})])],"derivedFrom":makeQuery(id+"F1.opExtrude","CAP_FACE",FACE,{"disambiguationData":[OSD([subQ10,subQ17,sQuery(id+"F0.wireOp",EDGE,"E1"),subQ16,subQ15,sQuery(id+"F0.wireOp",EDGE,"E9"),subQ1,subQ13,subQ0,subQ4,subQ8])],"isStart":false})})]});}
            var Q8;
            Q8=makeQuery(id+"F1.opExtrude","CAP_EDGE",EDGE,{"disambiguationData":[OSD([sQuery(id+"F0.wireOp",EDGE,"E0.top")])],"isStart":false});
            chamfer(context, id + "F12", {"entities" : qUnion([Q0, Q1, Q2, Q3, Q4, Q5, Q6, Q7, Q8]), "width" : 1.3 * mm, "tangentPropagation" : true});
        }
        {
            var Q0;
            Q0=makeQuery(id+"F4.opExtrude","SWEPT_EDGE",EDGE,{"disambiguationData":[OSD([sQuery(id+"F0.wireOp",EDGE,"E0.top"),sQuery(id+"F3.wireOp",EDGE,"E18.0")])]});
            var Q1;
            Q1=makeQuery(id+"F4.opExtrude","SWEPT_EDGE",EDGE,{"disambiguationData":[OSD([sQuery(id+"F3.wireOp",EDGE,"E18.0"),sQuery(id+"F3.wireOp",EDGE,"E19.0")])]});
            fillet(context, id + "F13", {"entities" : qUnion([Q0, Q1]), "radius" : 10 * mm, "tangentPropagation" : true, "allowEdgeOverflow" : false});
        }
        {
            var Q0;
            Q0=makeQuery(id+"F4.opExtrude","CAP_FACE",FACE,{"disambiguationData":[OSD([sQuery(id+"F0.wireOp",EDGE,"E0.top"),sQuery(id+"F0.wireOp",EDGE,"E1"),sQuery(id+"F0.wireOp",EDGE,"E3"),sQuery(id+"F0.wireOp",EDGE,"E12"),sQuery(id+"F3.wireOp",EDGE,"E18.0"),sQuery(id+"F3.wireOp",EDGE,"E19.0"),sQuery(id+"F3.wireOp",EDGE,"E20.0"),sQuery(id+"F3.wireOp",EDGE,"E21.0"),sQuery(id+"F3.wireOp",EDGE,"E23.0")])],"isStart":false});
            var sketch = newSketch(context, id + "F14", { "sketchPlane" : qUnion([Q0])});
            skLineSegment(sketch, "E44.0.0", {"start": v(-2.1, 16.5) * mm, "end": v(-4.77, 16.5) * mm});
            skArc(sketch, "E44.0.1", {"start": v(-4.77, 16.5) * mm, "mid": v(-9.32, 15.4) * mm, "end": v(-12.88, 12.36) * mm});
            skArc(sketch, "E44.0.2", {"start": v(-12.88, 12.36) * mm, "mid": v(-9.82, -10.8) * mm, "end": v(13.46, -9.05) * mm});
            skArc(sketch, "E44.0.3", {"start": v(13.46, -9.05) * mm, "mid": v(14.6, -7.56) * mm, "end": v(15.42, -5.88) * mm});
            skArc(sketch, "E44.0.4", {"start": v(15.42, -5.88) * mm, "mid": v(12.96, 10.2) * mm, "end": v(-2.1, 16.37) * mm});
            skLineSegment(sketch, "E44.0.5", {"start": v(-2.1, 16.37) * mm, "end": v(-2.1, 16.5) * mm});
            skLineSegment(sketch, "E45", {"start": v(0.64, -11.58) * mm, "end": v(0.64, -14.6) * mm});
            skLineSegment(sketch, "E46", {"start": v(3.93, -11.58) * mm, "end": v(3.93, -14.33) * mm});
            skCircle(sketch, "E47.0", {"center": v(0.9, 2.4) * mm, "radius": 10 * mm});
            skSolve(sketch);
        }
        {
            var Q0;
            {var subQ0=sQuery(id+"F14.wireOp",EDGE,"E45");Q0=makeQuery(id+"F14.imprint","IMPRINT",FACE,{"disambiguationData":[TD([[makeQuery(id+"F14.imprint","IMPRINT",EDGE,{"derivedFrom":subQ0}),1.0]])]});}
            extrude(context, id + "F15", {"entities" : qUnion([Q0]), "operationType" : NewBodyOperationType.REMOVE, "oppositeDirection" : true, "depth" : 3 * mm, "offsetDistance" : 25 * mm});
        }
        {
            var Q0;
            Q0=makeQuery(id+"F14.imprint","IMPRINT",FACE,{"disambiguationData":[TD([[makeQuery(id+"F14.imprint","IMPRINT",EDGE,{"derivedFrom":makeQuery(id+"F4.opExtrude","CAP_EDGE",EDGE,{"disambiguationData":[OSD([sQuery(id+"F3.wireOp",EDGE,"E20.0")])],"isStart":false})}),-1.0]])]});
            var Q1;
            Q1=makeQuery(id+"F14.imprint","IMPRINT",FACE,{"disambiguationData":[TD([[makeQuery(id+"F14.imprint","IMPRINT",EDGE,{"derivedFrom":sQuery(id+"F14.wireOp",EDGE,"E44.0.0")}),-1.0]])]});
            var Q2;
            {var subQ0=sQuery(id+"F14.wireOp",EDGE,"E45");Q2=makeQuery(id+"F14.imprint","IMPRINT",FACE,{"disambiguationData":[TD([[makeQuery(id+"F14.imprint","IMPRINT",EDGE,{"derivedFrom":subQ0}),1.0]])]});}
            extrude(context, id + "F16", {"entities" : qUnion([Q0, Q1, Q2]), "operationType" : NewBodyOperationType.ADD, "depth" : 1 * mm, "offsetDistance" : 25 * mm});
        }
        {
            var Q0;
            Q0=makeQuery(id+"F1.opExtrude","CAP_EDGE",EDGE,{"disambiguationData":[OSD([sQuery(id+"F0.wireOp",EDGE,"E1")])],"isStart":true});
            fillet(context, id + "F17", {"entities" : qUnion([Q0]), "radius" : 1 * mm, "tangentPropagation" : true, "allowEdgeOverflow" : false});
        }
        {
            var Q0;
            Q0=makeQuery(id+"F2.opExtrude","SWEPT_FACE",FACE,{"disambiguationData":[OSD([sQuery(id+"F0.wireOp",EDGE,"E4")])]});
            var sketch = newSketch(context, id + "F18", { "sketchPlane" : qUnion([Q0])});
            skCircle(sketch, "E48", {"center": v(-13.8, 4) * mm, "radius": 1.2 * mm});
            skPoint(sketch, "E48.centerSnap0", {"position": v(-16.5, 4) * mm});
            skCircle(sketch, "E49", {"center": v(-13.8, 4) * mm, "radius": 2.7 * mm});
            skSolve(sketch);
        }
        {
            var Q0;
            Q0=makeQuery(id+"F18.imprint","IMPRINT",FACE,{"disambiguationData":[TD([[makeQuery(id+"F18.imprint","IMPRINT",EDGE,{"derivedFrom":sQuery(id+"F18.wireOp",EDGE,"E48")}),-1.0]])]});
            extrude(context, id + "F19", {"entities" : qUnion([Q0]), "operationType" : NewBodyOperationType.ADD, "depth" : 2 * mm, "offsetDistance" : 25 * mm});
        }
        {
            var Q0;
            Q0=makeQuery(id+"F19.boolean.opBoolean","SPLIT",FACE,{"disambiguationData":[TD([makeQuery(id+"F19.opExtrude","SWEPT_FACE",FACE,{"disambiguationData":[OSD([sQuery(id+"F18.wireOp",EDGE,"E48")])]})])],"derivedFrom":makeQuery(id+"F2.opExtrude","SWEPT_FACE",FACE,{"disambiguationData":[OSD([sQuery(id+"F0.wireOp",EDGE,"E4")])]})});
            extrude(context, id + "F20", {"entities" : qUnion([Q0]), "operationType" : NewBodyOperationType.REMOVE, "oppositeDirection" : true, "depth" : 25 * mm, "offsetDistance" : 25 * mm});
        }
        {
            var Q0;
            Q0=makeQuery(id+"F19.opExtrude","CAP_EDGE",EDGE,{"disambiguationData":[OSD([sQuery(id+"F18.wireOp",EDGE,"E49")])],"isStart":true});
            var Q1;
            Q1=makeQuery(id+"F19.opExtrude","CAP_EDGE",EDGE,{"disambiguationData":[OSD([sQuery(id+"F18.wireOp",EDGE,"E49")])],"isStart":false});
            fillet(context, id + "F21", {"entities" : qUnion([Q0, Q1]), "radius" : 1 * mm, "tangentPropagation" : true, "allowEdgeOverflow" : false});
        }
    });
